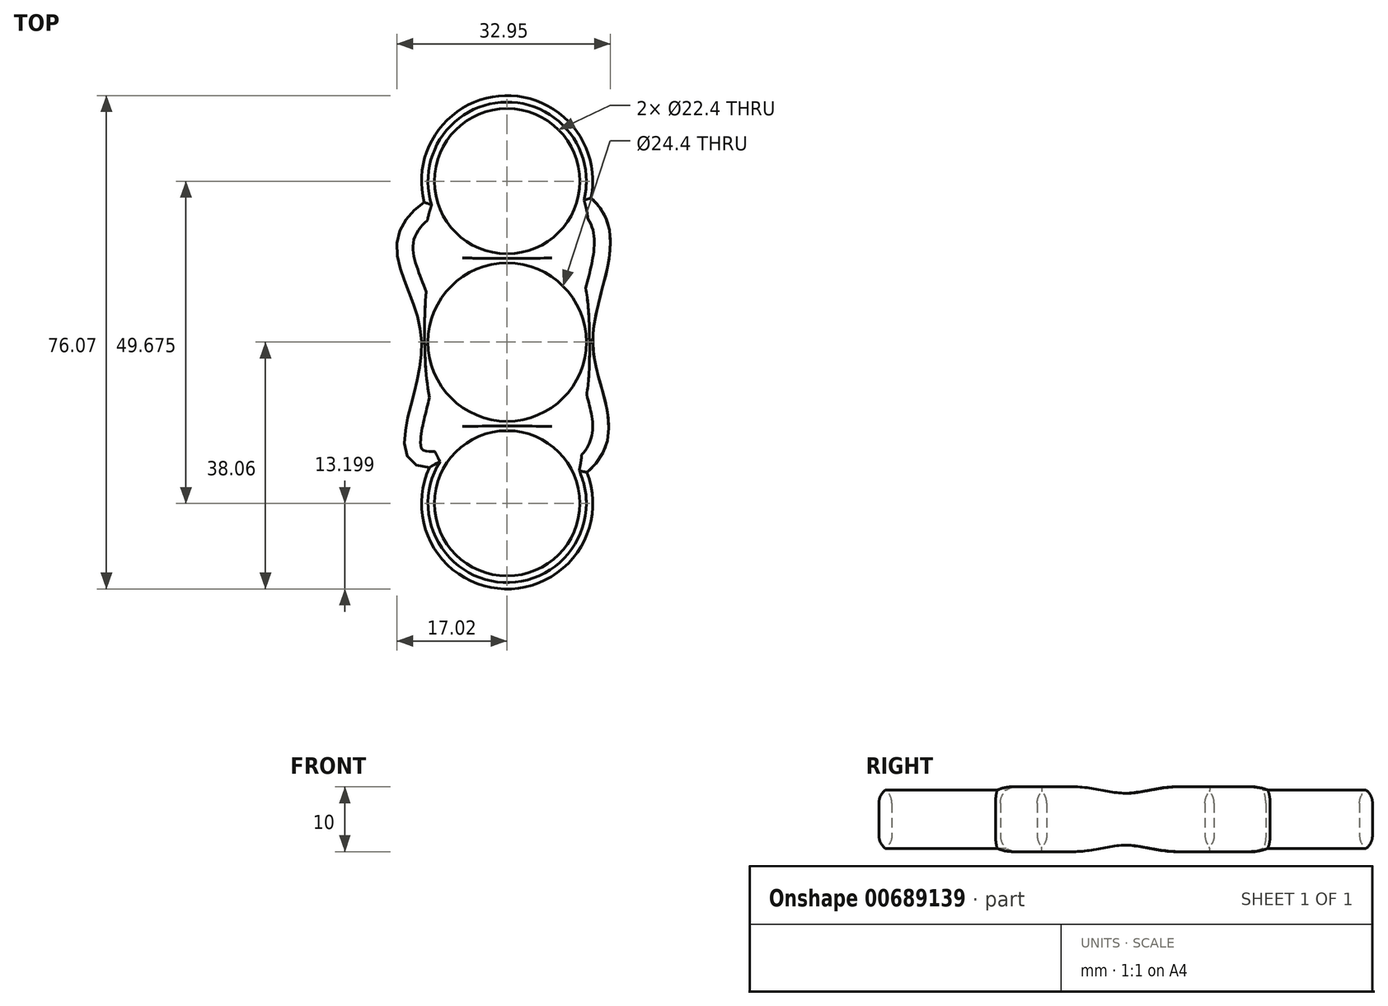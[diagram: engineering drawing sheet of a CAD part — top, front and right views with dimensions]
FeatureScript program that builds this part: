
annotation { "Feature Type Name" : "Feature", "Feature Type Description" : "" }
export const myFeature = defineFeature(function(context is Context, id is Id, definition is map)
    precondition{}
    {
        {
            var Q0;
            Q0=qCreatedBy(makeId("Top.planeOp"),FACE);
            var sketch = newSketch(context, id + "F0", { "sketchPlane" : qUnion([Q0])});
            skLineSegment(sketch, "E0", {"start": v(13.2, 0) * mm, "end": v(13.2, 0) * mm});
            skCircle(sketch, "E1", {"center": v(0, 24.81) * mm, "radius": 11.2 * mm});
            skArc(sketch, "E2", {"start": v(12.94, 22.23) * mm, "mid": v(-0.34, 38) * mm, "end": v(-12.8, 21.56) * mm});
            skCircle(sketch, "E3.1.0", {"center": v(0, -24.86) * mm, "radius": 11.2 * mm});
            skArc(sketch, "E3.1.1", {"start": v(-11.99, -19.34) * mm, "mid": v(-0.4, -38.05) * mm, "end": v(12.3, -20.1) * mm});
            skPoint(sketch, "E3.center", {"position": v(0, -0.02) * mm});
            skLineSegment(sketch, "E4", {"start": v(0, 38.01) * mm, "end": v(0, 36.01) * mm, "construction": true});
            skPoint(sketch, "E5.orphan", {"position": v(0, 52.32) * mm});
            skLineSegment(sketch, "E6.trimOffspring", {"start": v(0, -24.86) * mm, "end": v(0, -38.06) * mm, "construction": true});
            skFitSpline(sketch, "E7", {"points": [v(-12.8, 21.56) * mm, v(-13.2, 0) * mm, v(-11.99, -19.34) * mm], "startDerivative": vector(-53.25, -39.03) * mm, "endDerivative": vector(49.63, -2.08) * mm});
            skFitSpline(sketch, "E8", {"points": [v(12.94, 22.23) * mm, v(13.2, 0) * mm, v(12.3, -20.1) * mm], "startDerivative": vector(38.68, -34.6) * mm, "endDerivative": vector(-42.9, -38.62) * mm});
            skCircle(sketch, "E9", {"center": v(0, 0) * mm, "radius": 12.2 * mm});
            skSolve(sketch);
        }
        {
            var Q0;
            Q0=makeQuery(id+"F0.imprint","IMPRINT",FACE,{"disambiguationData":[TD([[makeQuery(id+"F0.imprint","IMPRINT",EDGE,{"derivedFrom":sQuery(id+"F0.wireOp",EDGE,"E1")}),-1.0]])]});
            extrude(context, id + "F1", {"entities" : qUnion([Q0]), "depth" : 10 * mm, "offsetDistance" : 25 * mm});
        }
        {
            var Q0;
            Q0=makeQuery(id+"F1.opExtrude","CAP_EDGE",EDGE,{"disambiguationData":[OSD([sQuery(id+"F0.wireOp",EDGE,"E3.1.1")])],"isStart":false});
            var Q1;
            Q1=makeQuery(id+"F1.opExtrude","CAP_EDGE",EDGE,{"disambiguationData":[OSD([sQuery(id+"F0.wireOp",EDGE,"E8")])],"isStart":false});
            var Q2;
            Q2=makeQuery(id+"F1.opExtrude","CAP_FACE",FACE,{"disambiguationData":[OSD([sQuery(id+"F0.wireOp",EDGE,"E1"),sQuery(id+"F0.wireOp",EDGE,"E2"),sQuery(id+"F0.wireOp",EDGE,"E3.1.0"),sQuery(id+"F0.wireOp",EDGE,"E3.1.1"),sQuery(id+"F0.wireOp",EDGE,"E7"),sQuery(id+"F0.wireOp",EDGE,"E8"),sQuery(id+"F0.wireOp",EDGE,"E9")])],"isStart":false});
            var Q3;
            Q3=makeQuery(id+"F1.opExtrude","CAP_FACE",FACE,{"disambiguationData":[OSD([sQuery(id+"F0.wireOp",EDGE,"E1"),sQuery(id+"F0.wireOp",EDGE,"E2"),sQuery(id+"F0.wireOp",EDGE,"E3.1.0"),sQuery(id+"F0.wireOp",EDGE,"E3.1.1"),sQuery(id+"F0.wireOp",EDGE,"E7"),sQuery(id+"F0.wireOp",EDGE,"E8"),sQuery(id+"F0.wireOp",EDGE,"E9")])],"isStart":true});
            fillet(context, id + "F2", {"entities" : qUnion([Q0, Q1, Q2, Q3]), "radius" : 2.5 * mm, "tangentPropagation" : true, "allowEdgeOverflow" : false});
        }
    });
